# Revit family: 81919001
name_source: partatom
category: Plumbing Fixtures
revit_build: Autodesk Revit 2017 (Build: 20181011_1645(x64)
units: mm (PartAtom-declared; Revit-internal decimal feet)

## family parameters
Always vertical = Yes
Cut with Voids When Loaded = No
OmniClass Number = 23.45.55.00
OmniClass Title = Sanitary Faucets, Wastes
Part Type = Normal
Room Calculation Point = No
Round Connector Dimension = Use Diameter
Shared = No
Work Plane-Based = No

## types (1)
- 81919001 Cover part for shower faucet, 3 V
    2D/3D/BIM Files URL = http://static.hansa.com
    Advanced Features = BLUECLICK, adjustable settings
    Approval ABP = PA-IX 29283/IBB
    AssetType = Fixed
    Automatic Flush = off (off/6/12/18/24/30/36/48/60/72 h)
    Automatic Flush Period = 30 s (30/60/90/120/180/240/300/360/480/600 s)
    BIMObjectName = 81919001
    Battery = AA 1.5 V Lithium x 2
    BodyMaterial = Brass
    Brand = Oras
    Catalog Drawing URL = http://static.hansa.com
    Category = Bathroom, shower, public & semi-public
    Class = Tiptronic, trim kit, battery-operated, thermostatic
    CloseOffRating = 0
    Color = Chrome
    ConvergoRefNr = 0087-1905-0048-FI
    Customs Code = 84818011
    Dimension Drawing URL = http://static.hansa.com
    DurationUnit = Year
    EAN Number = 4057304004889
    EMC Directive = 2014/30/EU
    Electronic Parts = Solenoid valve;Control unit;Signal lights;Low battery indication
    Extensions = Push button
    FDV Document URL = http://www.hansa.com
    FaucetMainMaterial = Brass
    Features = Tiptronic, trim kit, battery-operated, thermostatic
    Finish = Polished
    Flow = Limitation option for maximum flow rate
    Flow Drawing URL = http://static.hansa.com
    Flow Rate At 300kPa = 0.2 L/s
    FlowCoefficient = 0
    Group = Shower faucets
    IfcExportAs = IfcValveType
    IfcExportType = FAUCET
    Installation Type = Wall mounted for concealed unit
    Installation and Maintenance = http://static.hansa.com
    ManufacterURL = http://www.hansa.com
    Manufacturer = Hansa
    ManufacturerName = Hansa
    Market = AUT;BEL;CZE;DEU;ESP;FRA;INT;NLD;SVK
    Material = Brass
    Max Flow Period = 45.0 s
    Max. Hot Water Supply = 70 °C
    Model = 81919001 Cover part for shower faucet, 3 V
    ModelReference = 81919001
    NBSDescription = Water supply fittings for baths
    NBSReference = 45-35-70/315
    Name = 81919001 Cover part for shower faucet, 3 V
    Name_en = 81919001 Cover part for shower faucet, 3 V
    NominalDepth = 87 mm  [stored 0.285433 ft]
    NominalHeight = 170 mm  [stored 0.557743 ft]
    NominalWidth = 170 mm  [stored 0.557743 ft]
    Operating Voltage = 3 V
    Package Weight = 1.8946 kg
    Package external Dimensions = 204 x 186 x 174
    Product Code = 81919001
    Product Datasheet = http://www.hansa.com
    Product Family = HANSAELECTRA
    Product Image URL = http://static.hansa.com
    Product URL = http://static.hansa.com
    Protection Class = IP 55
    Shape = Sculptured
    Size = 170x170x90 mm
    Spare Parts = http://static.hansa.com
    Temperature = Thermostatic temperature control;Temperature limiter;Thermostatic safety stop at 38°C
    URL ABP = http://static.hansa.com
    Uniclass2 = Pr_40_30_96_78
    Uniclass2015Description = Shower manual water supply sets
    Uniclass2015Reference = Pr_40_20_87_78
    Version = 1
    VersionDate = 09/04/2019
    WarrantyDescription = http://warranty.hansa.com
    WarrantyDurationUnit = Year
    WorkingPressure = 100 - 1000 kPa

note: [stored X ft] marks values corroborated as IEEE doubles in the binary element streams (Revit-internal decimal feet)

## geometry (parser evidence)
native form markers: Sweep x5
no freeform markers — native parametric forms only
